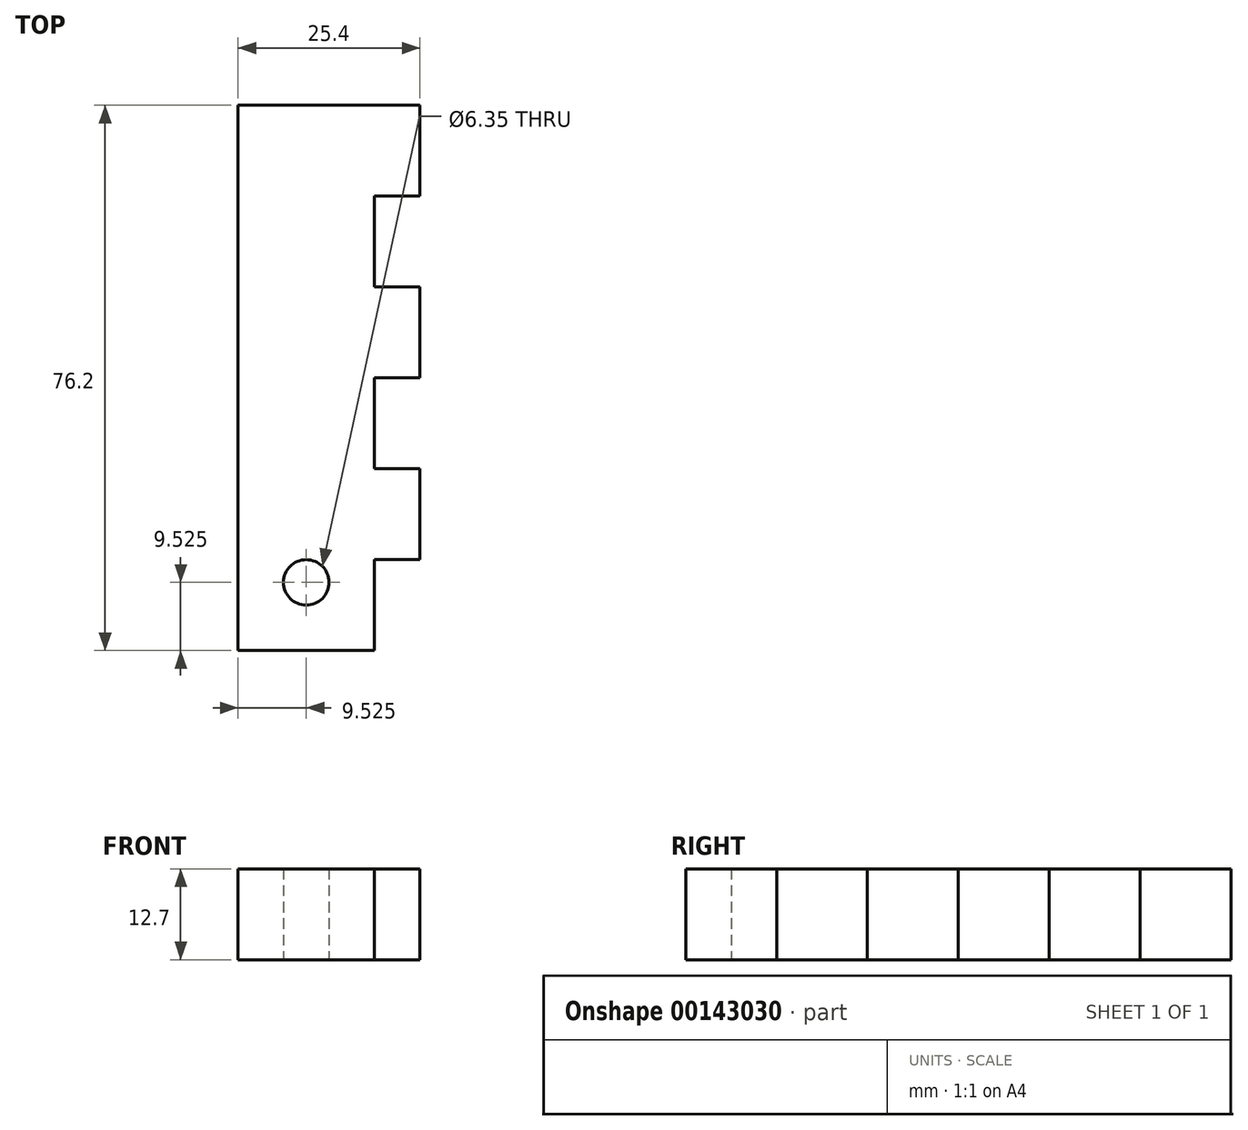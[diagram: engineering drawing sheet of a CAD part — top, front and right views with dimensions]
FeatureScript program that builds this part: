
annotation { "Feature Type Name" : "Feature", "Feature Type Description" : "" }
export const myFeature = defineFeature(function(context is Context, id is Id, definition is map)
    precondition{}
    {
        {
            var Q0;
            Q0=qCreatedBy(makeId("Top.planeOp"),FACE);
            var sketch = newSketch(context, id + "F0", { "sketchPlane" : qUnion([Q0])});
            skLineSegment(sketch, "E0.bottom", {"start": v(0, 0) * mm, "end": v(19.05, 0) * mm});
            skLineSegment(sketch, "E0.top", {"start": v(0, 76.2) * mm, "end": v(19.05, 76.2) * mm});
            skLineSegment(sketch, "E0.left", {"start": v(0, 0) * mm, "end": v(0, 76.2) * mm});
            skLineSegment(sketch, "E0.right", {"start": v(19.05, 0) * mm, "end": v(19.05, 12.7) * mm});
            skCircle(sketch, "E1", {"center": v(9.52, 9.53) * mm, "radius": 3.18 * mm});
            skLineSegment(sketch, "E2.bottom", {"start": v(19.05, 76.2) * mm, "end": v(25.4, 76.2) * mm});
            skLineSegment(sketch, "E2.top", {"start": v(19.05, 63.5) * mm, "end": v(25.4, 63.5) * mm});
            skLineSegment(sketch, "E2.right", {"start": v(25.4, 76.2) * mm, "end": v(25.4, 63.5) * mm});
            skLineSegment(sketch, "E3.bottom", {"start": v(19.05, 50.8) * mm, "end": v(25.4, 50.8) * mm});
            skLineSegment(sketch, "E3.top", {"start": v(19.05, 38.1) * mm, "end": v(25.4, 38.1) * mm});
            skLineSegment(sketch, "E3.right", {"start": v(25.4, 50.8) * mm, "end": v(25.4, 38.1) * mm});
            skLineSegment(sketch, "E4.bottom", {"start": v(19.05, 25.4) * mm, "end": v(25.4, 25.4) * mm});
            skLineSegment(sketch, "E4.top", {"start": v(19.05, 12.7) * mm, "end": v(25.4, 12.7) * mm});
            skLineSegment(sketch, "E4.right", {"start": v(25.4, 25.4) * mm, "end": v(25.4, 12.7) * mm});
            skLineSegment(sketch, "E5.trimOffspring", {"start": v(19.05, 25.4) * mm, "end": v(19.05, 38.1) * mm});
            skLineSegment(sketch, "E6.trimOffspring", {"start": v(19.05, 50.8) * mm, "end": v(19.05, 63.5) * mm});
            skSolve(sketch);
        }
        {
            var Q0;
            Q0=makeQuery(id+"F0.imprint","IMPRINT",FACE,{"disambiguationData":[TD([[makeQuery(id+"F0.imprint","IMPRINT",EDGE,{"derivedFrom":sQuery(id+"F0.wireOp",EDGE,"E0.bottom")}),1.0]])]});
            extrude(context, id + "F1", {"entities" : qUnion([Q0]), "depth" : 12.7 * mm});
        }
    });
